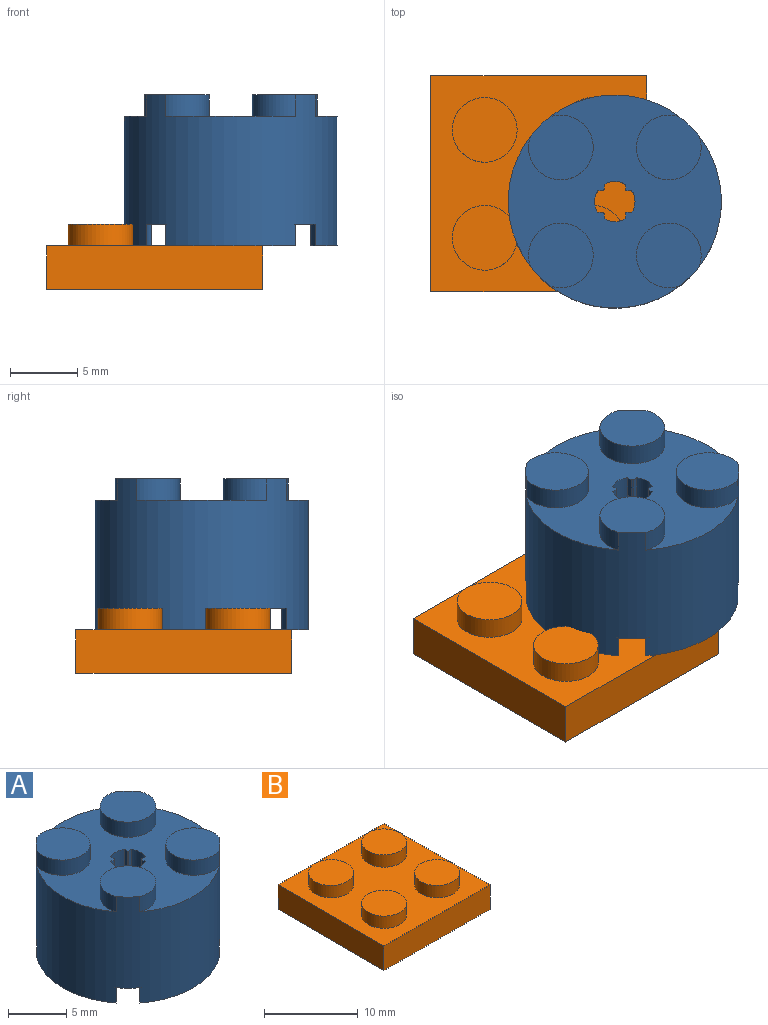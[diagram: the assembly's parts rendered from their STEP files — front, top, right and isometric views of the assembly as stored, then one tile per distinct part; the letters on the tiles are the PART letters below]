
ASSEMBLY  parts=2 mates=1
PART A: 55 faces, bbox 15.8x15.8x11.2 mm
  f0: plane 9.66x2.01mm, normal (0,0,-1), area 10.8mm2, adj f19,f23,f37,f54
  f1: plane 9.66x2.01mm, normal (0,0,-1), area 10.8mm2, adj f14,f22,f37,f54
  f2: plane 9.66x2.01mm, normal (0,0,-1), area 10.8mm2, adj f16,f20,f37,f54
  f3: plane 9.66x2.01mm, normal (0,0,-1), area 10.8mm2, adj f13,f17,f37,f54
  f4: plane 15.8x15.8mm, normal (0,0,1), area 118mm2, adj f9,f10,f11,f12,f40,f42,f43,f44
  f5: plane 4.8x4.8mm, normal (0,0,1), area 17.9mm2, adj f11,f54
  f6: plane 4.8x4.8mm, normal (0,0,1), area 17.9mm2, adj f9,f54
  f7: plane 4.8x4.8mm, normal (0,0,1), area 17.9mm2, adj f10,f54
  f8: plane 4.8x4.8mm, normal (0,0,1), area 17.9mm2, adj f12,f54
  f9: cylinder r=2.4mm len=4.8mm, axis (0,0,-1), area 20.8mm2, adj f4,f6,f54
  f10: cylinder r=2.4mm len=4.8mm, axis (0,0,-1), area 20.8mm2, adj f4,f7,f54
  f11: cylinder r=2.4mm len=4.8mm, axis (0,0,-1), area 20.8mm2, adj f4,f5,f54
  f12: cylinder r=2.4mm len=4.8mm, axis (0,0,-1), area 20.8mm2, adj f4,f8,f54
  f13: cylinder r=2.4mm len=2.31mm, axis (0,0,-1), area 3.9mm2, adj f3,f15,f37,f54
  f14: cylinder r=2.4mm len=2.31mm, axis (0,0,-1), area 3.9mm2, adj f1,f15,f37,f54
  f15: plane 3.89x3.89mm, normal (0,0,-1), area 6mm2, adj f13,f14,f37,f54
  f16: cylinder r=2.4mm len=2.31mm, axis (0,0,-1), area 3.9mm2, adj f2,f18,f37,f54
  f17: cylinder r=2.4mm len=2.31mm, axis (0,0,-1), area 3.9mm2, adj f3,f18,f37,f54
  f18: plane 3.89x3.89mm, normal (0,0,-1), area 6mm2, adj f16,f17,f37,f54
  f19: cylinder r=2.4mm len=2.31mm, axis (0,0,-1), area 3.9mm2, adj f0,f21,f37,f54
  f20: cylinder r=2.4mm len=2.31mm, axis (0,0,-1), area 3.9mm2, adj f2,f21,f37,f54
  f21: plane 3.89x3.89mm, normal (0,0,-1), area 6mm2, adj f19,f20,f37,f54
  f22: cylinder r=2.4mm len=2.31mm, axis (0,0,-1), area 3.9mm2, adj f1,f24,f37,f54
  f23: cylinder r=2.4mm len=2.31mm, axis (0,0,-1), area 3.9mm2, adj f0,f24,f37,f54
  f24: plane 3.89x3.89mm, normal (0,0,-1), area 6mm2, adj f22,f23,f37,f54
  f25: plane 0.47x0.47mm, normal (0,0,-1), area 0.1mm2, adj f40,f44,f45,f46
  f26: plane 0.47x0.47mm, normal (0,0,-1), area 0.1mm2, adj f40,f47,f48,f49
  f27: plane 0.47x0.47mm, normal (0,0,-1), area 0.1mm2, adj f40,f50,f51,f52
  f28: plane 12.8x12.8mm, normal (0,0,-1), area 107.7mm2, adj f33,f34,f35,f36,f37,f39
  f29: plane 1.6x1.6mm, normal (0,0,-1), area 2mm2, adj f35,f37
  f30: plane 1.6x1.6mm, normal (0,0,-1), area 2mm2, adj f33,f37
  f31: plane 1.6x1.6mm, normal (0,0,-1), area 2mm2, adj f34,f37
  f32: plane 1.6x1.6mm, normal (0,0,-1), area 2mm2, adj f36,f37
  f33: cylinder r=0.8mm len=1.6mm, axis (0,0,-1), area 7mm2, adj f28,f30,f37
  f34: cylinder r=0.8mm len=1.6mm, axis (0,0,-1), area 7mm2, adj f28,f31,f37
  f35: cylinder r=0.8mm len=1.6mm, axis (0,0,-1), area 7mm2, adj f28,f29,f37
  f36: cylinder r=0.8mm len=1.6mm, axis (0,0,-1), area 7mm2, adj f28,f32,f37
  f37: cylinder r=6.4mm len=12.8mm, axis (0,0,-1), area 294.5mm2, adj f0,f1,f2,f3,f13,f14,f15,f16
  f38: plane 4.07x4.07mm, normal (0,0,-1), area 5.9mm2, adj f39,f40
  f39: cylinder r=2.03mm len=8mm, axis (0,0,1), area 102.3mm2, adj f28,f38
  f40: cylinder r=1.5mm len=9.6mm, axis (0,0,1), area 86.2mm2, adj f4,f25,f26,f27,f38,f41,f43,f44
  f41: plane 0.47x0.47mm, normal (0,0,-1), area 0.1mm2, adj f40,f42,f43,f53
  f42: cylinder r=0.1mm len=1.6mm, axis (0,0,1), area 0.3mm2, adj f4,f41,f43,f53
  f43: plane 1.6x0.37mm, normal (-1,0,0), area 0.6mm2, adj f4,f40,f41,f42
  f44: plane 1.6x0.37mm, normal (1,0,0), area 0.6mm2, adj f4,f25,f40,f45
  f45: cylinder r=0.1mm len=1.6mm, axis (0,0,1), area 0.3mm2, adj f4,f25,f44,f46
  f46: plane 1.6x0.37mm, normal (0,-1,0), area 0.6mm2, adj f4,f25,f40,f45
  f47: plane 1.6x0.37mm, normal (0,1,0), area 0.6mm2, adj f4,f26,f40,f48
  f48: cylinder r=0.1mm len=1.6mm, axis (0,0,1), area 0.3mm2, adj f4,f26,f47,f49
  f49: plane 1.6x0.37mm, normal (1,0,0), area 0.6mm2, adj f4,f26,f40,f48
  f50: plane 1.6x0.37mm, normal (-1,0,0), area 0.6mm2, adj f4,f27,f40,f51
  f51: cylinder r=0.1mm len=1.6mm, axis (0,0,1), area 0.3mm2, adj f4,f27,f50,f52
  f52: plane 1.6x0.37mm, normal (0,1,0), area 0.6mm2, adj f4,f27,f40,f51
  f53: plane 1.6x0.37mm, normal (0,-1,0), area 0.6mm2, adj f4,f40,f41,f42
  f54: cylinder r=7.9mm len=15.8mm, axis (0,0,-1), area 476.5mm2, adj f0,f1,f2,f3,f4,f5,f6,f7
PART B: 31 faces, bbox 16x16x4.8 mm
  f0: plane 16x16mm, normal (0,0,-1), area 92.2mm2, adj f1,f2,f3,f4,f14,f15,f16,f17
  f1: plane 16x3.2mm, normal (-1,0,0), area 51.2mm2, adj f0,f2,f4,f5
  f2: plane 16x3.2mm, normal (0,-1,0), area 51.2mm2, adj f0,f1,f3,f5
  f3: plane 16x3.2mm, normal (1,0,0), area 51.2mm2, adj f0,f2,f4,f5
  f4: plane 16x3.2mm, normal (0,1,0), area 51.2mm2, adj f0,f1,f3,f5
  f5: plane 16x16mm, normal (0,0,1), area 183.6mm2, adj f1,f2,f3,f4,f6,f8,f10,f12
  f6: cylinder r=2.4mm len=4.8mm, axis (0,0,-1), area 24.1mm2, adj f5,f7
  f7: plane 4.8x4.8mm, normal (0,0,1), area 18.1mm2, adj f6
  f8: cylinder r=2.4mm len=4.8mm, axis (0,0,-1), area 24.1mm2, adj f5,f9
  f9: plane 4.8x4.8mm, normal (0,0,1), area 18.1mm2, adj f8
  f10: cylinder r=2.4mm len=4.8mm, axis (0,0,-1), area 24.1mm2, adj f5,f11
  f11: plane 4.8x4.8mm, normal (0,0,1), area 18.1mm2, adj f10
  f12: cylinder r=2.4mm len=4.8mm, axis (0,0,-1), area 24.1mm2, adj f5,f13
  f13: plane 4.8x4.8mm, normal (0,0,1), area 18.1mm2, adj f12
  f14: plane 12.8x1.6mm, normal (1,0,0), area 20.5mm2, adj f0,f15,f17,f18
  f15: plane 12.8x1.6mm, normal (0,1,0), area 20.5mm2, adj f0,f14,f16,f18
  f16: plane 12.8x1.6mm, normal (-1,0,0), area 20.5mm2, adj f0,f15,f17,f18
  f17: plane 12.8x1.6mm, normal (0,-1,0), area 20.5mm2, adj f0,f14,f16,f18
  f18: plane 12.8x12.8mm, normal (0,0,-1), area 122.5mm2, adj f14,f15,f16,f17,f19,f21,f23,f25
  f19: cylinder r=0.8mm len=1.6mm, axis (0,0,-1), area 8mm2, adj f18,f20
  f20: plane 1.6x1.6mm, normal (0,0,-1), area 2mm2, adj f19
  f21: cylinder r=0.8mm len=1.6mm, axis (0,0,-1), area 8mm2, adj f18,f22
  f22: plane 1.6x1.6mm, normal (0,0,-1), area 2mm2, adj f21
  f23: cylinder r=0.8mm len=1.6mm, axis (0,0,-1), area 8mm2, adj f18,f24
  f24: plane 1.6x1.6mm, normal (0,0,-1), area 2mm2, adj f23
  f25: cylinder r=0.8mm len=1.6mm, axis (0,0,-1), area 8mm2, adj f18,f26
  f26: plane 1.6x1.6mm, normal (0,0,-1), area 2mm2, adj f25
  f27: plane 6.51x6.51mm, normal (0,0,-1), area 15.2mm2, adj f28,f29
  f28: cylinder r=3.26mm len=6.51mm, axis (0,0,1), area 32.7mm2, adj f18,f27
  f29: cylinder r=2.4mm len=4.8mm, axis (0,0,1), area 24.1mm2, adj f27,f30
  f30: plane 4.8x4.8mm, normal (0,0,-1), area 18.1mm2, adj f29
PLACE A t=(5.64,-1.32,3.2)mm
PLACE B at identity fixed
MATE planar A.f37 <-> B.f28  axis (0,0,-1) through (13.64,6.68,3.2)mm
